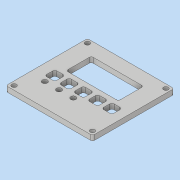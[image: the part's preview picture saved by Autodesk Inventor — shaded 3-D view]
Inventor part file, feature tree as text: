
AUTODESK INVENTOR PART (.ipt)
format: ipt  version: 2018 (Build 220112000, 112)  size: 205,824 bytes
history: native  units: mm
features: sketch x4, reference x3, other x3, extrude x2, hole x2, fillet x2, projected_geometry x1
ambient origin geometry x8: Origin, YZ Plane, XZ Plane, XY Plane, X Axis, Y Axis, Z Axis, Center Point
bodies: Volumenkörper1 (feature_tree)
feature tree (17):
  extrude  "Extrusion1"  Depth=80.0mm
  extrude  "Extrusion3"  Depth=5.0mm
  hole  "Bohrung2"  [1 undecoded]
  hole  "Bohrung3"  [1 undecoded]
  fillet  "Rundung2"  Radius=10.0mm
  fillet  "Rundung1"  Radius=10.0mm
  sketch  "Skizze1"  dims[d0=85.0mm d1=80.0mm]
  sketch  "Skizze3"  dims[d2=5.0mm d3=0.0mm d9=70.0mm]
  sketch  "Skizze5"  dims[d10=62.0mm d12=51.3mm]
  projected_geometry  "Projizierte Kontur1"
  sketch  "Skizze6"  dims[d13=24.7mm d14=4.15mm d15=10.0mm d16=10.0mm d21=8.0mm d22=23.5mm d23=14.0mm d24=14.0mm d25=14.0mm d26=14.0mm d27=5.0mm d28=0.0mm d29=2.1mm d39=4.0mm d40=4.5mm d41=6.0mm d42=4.0mm d43=2.0mm d44=90.0deg d45=8.0mm d46=20.594885mm d47=2.0mm d48=5.0mm d49=6.0mm d50=4.0mm d51=2.0mm d52=90.0deg d53=8.0mm d54=20.594885mm]
  reference  "Referenz7"
  reference  "Referenz8"
  reference  "Referenz9"
  other  "<userpath>\Documents\Waage\CAD\Main.iam"
  other  "Main.iam"
  other  "WaagePCB:1"
note: 2 required parameter values undecoded (feature->parameter linkage not recoverable at this tier; creation-order binding heuristic only, values carry confidence <= 0.55)
